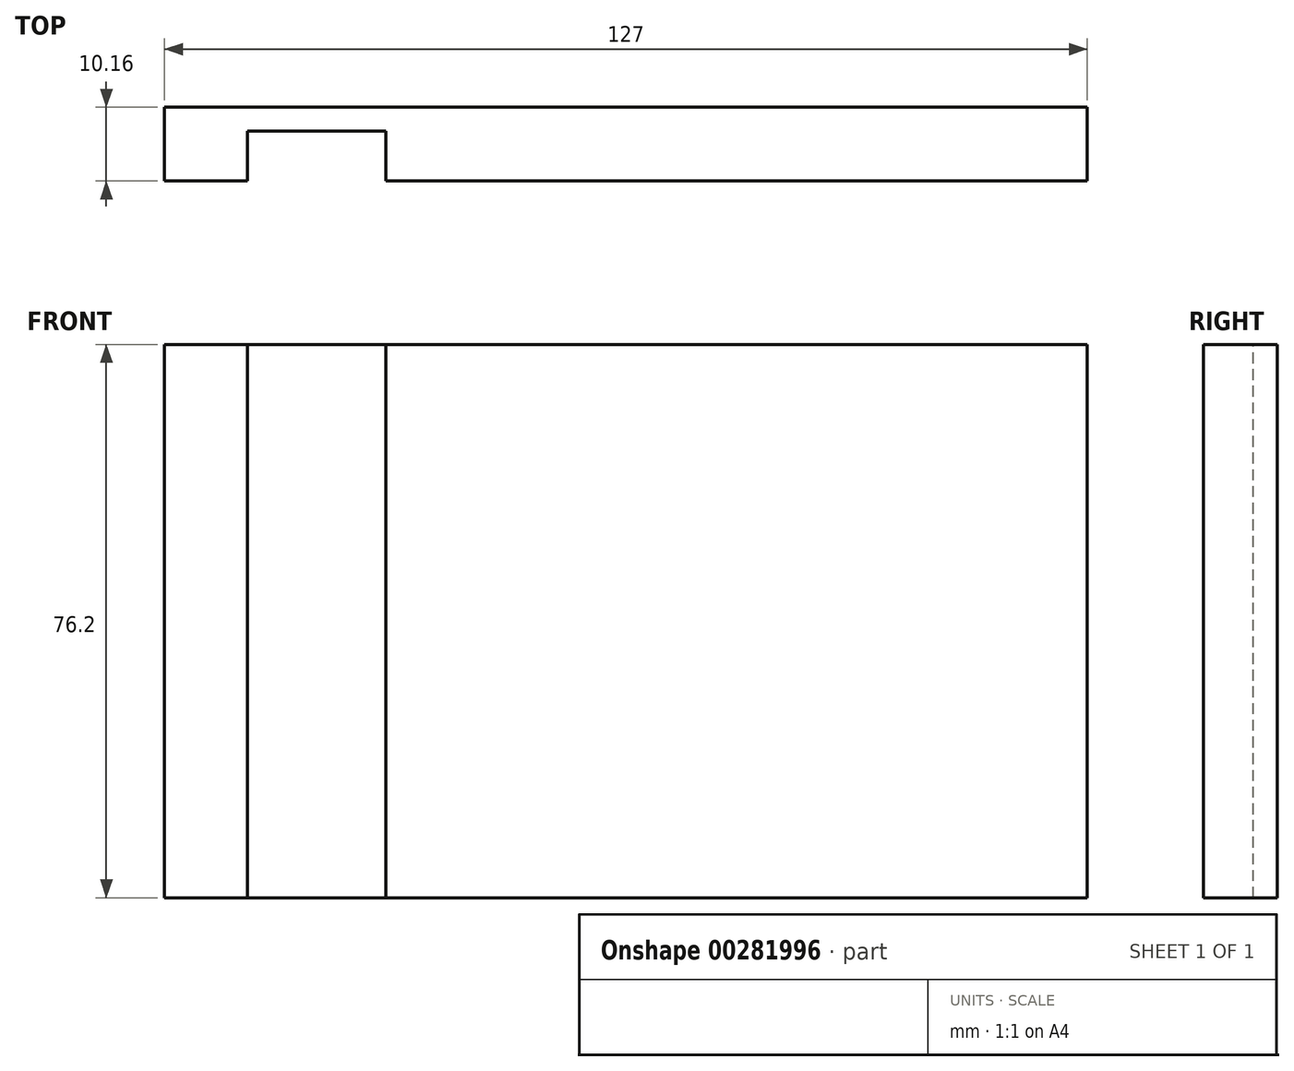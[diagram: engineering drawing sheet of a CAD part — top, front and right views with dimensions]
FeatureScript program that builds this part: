
annotation { "Feature Type Name" : "Feature", "Feature Type Description" : "" }
export const myFeature = defineFeature(function(context is Context, id is Id, definition is map)
    precondition{}
    {
        {
            var Q0;
            Q0=qCreatedBy(makeId("Front.planeOp"),FACE);
            var sketch = newSketch(context, id + "F0", { "sketchPlane" : qUnion([Q0])});
            skLineSegment(sketch, "E0.bottom", {"start": v(0, 0) * mm, "end": v(-127, 0) * mm});
            skLineSegment(sketch, "E0.top", {"start": v(0, 76.2) * mm, "end": v(-127, 76.2) * mm});
            skLineSegment(sketch, "E0.left", {"start": v(0, 0) * mm, "end": v(0, 76.2) * mm});
            skLineSegment(sketch, "E0.right", {"start": v(-127, 0) * mm, "end": v(-127, 76.2) * mm});
            skSolve(sketch);
        }
        {
            var Q0;
            Q0=makeQuery(id+"F0.imprint","IMPRINT",FACE,{"disambiguationData":[TD([[makeQuery(id+"F0.imprint","IMPRINT",EDGE,{"derivedFrom":sQuery(id+"F0.wireOp",EDGE,"E0.bottom")}),-1.0]])]});
            extrude(context, id + "F1", {"entities" : qUnion([Q0]), "depth" : 10.16 * mm});
        }
        {
            var Q0;
            Q0=makeQuery(id+"F1.opExtrude","SWEPT_FACE",FACE,{"disambiguationData":[OSD([sQuery(id+"F0.wireOp",EDGE,"E0.top")])]});
            var sketch = newSketch(context, id + "F2", { "sketchPlane" : qUnion([Q0])});
            skLineSegment(sketch, "E1.bottom", {"start": v(-112.92, -10.16) * mm, "end": v(-93.87, -10.16) * mm});
            skLineSegment(sketch, "E1.top", {"start": v(-112.92, -4.08) * mm, "end": v(-93.87, -4.08) * mm});
            skLineSegment(sketch, "E1.left", {"start": v(-112.92, -10.16) * mm, "end": v(-112.92, -4.08) * mm});
            skLineSegment(sketch, "E1.right", {"start": v(-93.87, -10.16) * mm, "end": v(-93.87, -4.08) * mm});
            skSolve(sketch);
        }
        {
            var Q0;
            Q0=makeQuery(id+"F2.imprint","IMPRINT",FACE,{"disambiguationData":[TD([[makeQuery(id+"F2.imprint","IMPRINT",EDGE,{"derivedFrom":sQuery(id+"F2.wireOp",EDGE,"E1.bottom")}),-1.0]])]});
            extrude(context, id + "F3", {"entities" : qUnion([Q0]), "operationType" : NewBodyOperationType.REMOVE, "oppositeDirection" : true, "depth" : 25.4 * mm});
        }
        {
            var Q0;
            Q0=makeQuery(id+"F3.boolean.opBoolean","COPY",FACE,{"derivedFrom":makeQuery(id+"F3.opExtrude","CAP_FACE",FACE,{"disambiguationData":[OSD([sQuery(id+"F2.wireOp",EDGE,"E1.bottom"),sQuery(id+"F2.wireOp",EDGE,"E1.top"),sQuery(id+"F2.wireOp",EDGE,"E1.left"),sQuery(id+"F2.wireOp",EDGE,"E1.right")])],"isStart":false})});
            extrude(context, id + "F4", {"entities" : qUnion([Q0]), "operationType" : NewBodyOperationType.REMOVE, "oppositeDirection" : true, "depth" : 25.4 * mm});
        }
        {
            var Q0;
            Q0=makeQuery(id+"F4.boolean.opBoolean","COPY",FACE,{"derivedFrom":makeQuery(id+"F4.opExtrude","CAP_FACE",FACE,{"disambiguationData":[OSD([sQuery(id+"F2.wireOp",EDGE,"E1.bottom"),sQuery(id+"F2.wireOp",EDGE,"E1.top"),sQuery(id+"F2.wireOp",EDGE,"E1.left"),sQuery(id+"F2.wireOp",EDGE,"E1.right")])],"isStart":false})});
            extrude(context, id + "F5", {"entities" : qUnion([Q0]), "operationType" : NewBodyOperationType.ADD, "depth" : 50.8 * mm});
        }
        {
            var Q0;
            Q0=makeQuery(id+"F5.boolean.opBoolean","MERGE",FACE,{"derivedFrom":[makeQuery(id+"F1.opExtrude","SWEPT_FACE",FACE,{"disambiguationData":[OSD([sQuery(id+"F0.wireOp",EDGE,"E0.top")])]}),makeQuery(id+"F5.opExtrude","CAP_FACE",FACE,{"disambiguationData":[OSD([sQuery(id+"F2.wireOp",EDGE,"E1.bottom"),sQuery(id+"F2.wireOp",EDGE,"E1.top"),sQuery(id+"F2.wireOp",EDGE,"E1.left"),sQuery(id+"F2.wireOp",EDGE,"E1.right")])],"isStart":false})]});
            var sketch = newSketch(context, id + "F6", { "sketchPlane" : qUnion([Q0])});
            skLineSegment(sketch, "E2.bottom", {"start": v(-96.52, -10.16) * mm, "end": v(-115.57, -10.16) * mm});
            skLineSegment(sketch, "E2.top", {"start": v(-96.52, -3.3) * mm, "end": v(-115.57, -3.3) * mm});
            skLineSegment(sketch, "E2.left", {"start": v(-96.52, -10.16) * mm, "end": v(-96.52, -3.3) * mm});
            skLineSegment(sketch, "E2.right", {"start": v(-115.57, -10.16) * mm, "end": v(-115.57, -3.3) * mm});
            skSolve(sketch);
        }
        {
            var Q0;
            Q0=makeQuery(id+"F6.imprint","IMPRINT",FACE,{"disambiguationData":[TD([[makeQuery(id+"F6.imprint","IMPRINT",EDGE,{"derivedFrom":sQuery(id+"F6.wireOp",EDGE,"E2.bottom")}),-1.0]])]});
            extrude(context, id + "F7", {"entities" : qUnion([Q0]), "operationType" : NewBodyOperationType.REMOVE, "oppositeDirection" : true, "depth" : 127 * mm});
        }
    });
